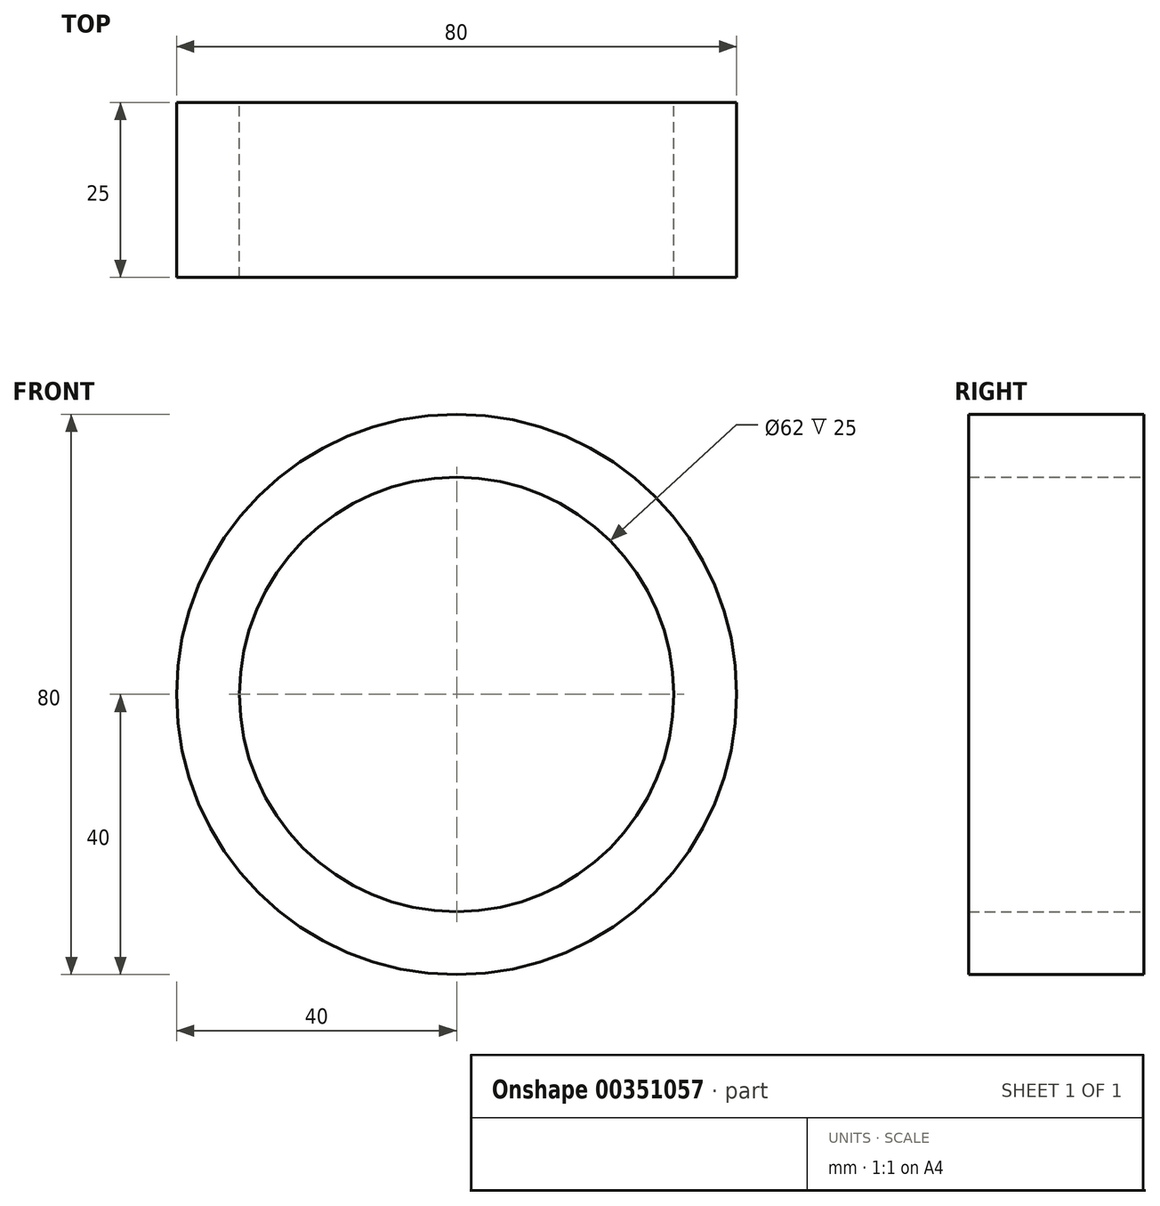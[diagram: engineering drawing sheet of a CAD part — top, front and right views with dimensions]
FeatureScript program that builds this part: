
annotation { "Feature Type Name" : "Feature", "Feature Type Description" : "" }
export const myFeature = defineFeature(function(context is Context, id is Id, definition is map)
    precondition{}
    {
        {
            var Q0;
            Q0=qCreatedBy(makeId("Front.planeOp"),FACE);
            var sketch = newSketch(context, id + "F0", { "sketchPlane" : qUnion([Q0])});
            skCircle(sketch, "E0", {"center": v(0, 0) * mm, "radius": 40 * mm});
            skCircle(sketch, "E1", {"center": v(0, 0) * mm, "radius": 31 * mm});
            skCircle(sketch, "E2", {"center": v(0, 0) * mm, "radius": 7.5 * mm});
            skCircle(sketch, "E3", {"center": v(0, 0) * mm, "radius": 2.5 * mm});
            skLineSegment(sketch, "E4", {"start": v(0, 0) * mm, "end": v(0, 40) * mm});
            skLineSegment(sketch, "E5", {"start": v(0, 0) * mm, "end": v(40, 0) * mm});
            skLineSegment(sketch, "E6", {"start": v(0, 0) * mm, "end": v(0, -40) * mm});
            skLineSegment(sketch, "E7", {"start": v(0, 0) * mm, "end": v(-40, 0) * mm});
            skLineSegment(sketch, "E8.0", {"start": v(5, 0) * mm, "end": v(5, 40) * mm});
            skLineSegment(sketch, "E9.0", {"start": v(-5, 0) * mm, "end": v(-5, 40) * mm});
            skLineSegment(sketch, "E10.0", {"start": v(0, 5) * mm, "end": v(-40, 5) * mm});
            skLineSegment(sketch, "E11.0", {"start": v(0, -5) * mm, "end": v(-40, -5) * mm});
            skLineSegment(sketch, "E12.0", {"start": v(-5, 0) * mm, "end": v(-5, -40) * mm});
            skLineSegment(sketch, "E13.0", {"start": v(5, 0) * mm, "end": v(5, -40) * mm});
            skLineSegment(sketch, "E14.0", {"start": v(0, -5) * mm, "end": v(40, -5) * mm});
            skLineSegment(sketch, "E15.0", {"start": v(0, 5) * mm, "end": v(40, 5) * mm});
            skSolve(sketch);
        }
        {
            var Q0;
            {var subQ0=sQuery(id+"F0.wireOp",EDGE,"E4");var subQ1=sQuery(id+"F0.wireOp",EDGE,"E0");var subQ2=makeQuery(id+"F0.imprint","INTERSECT",VERTEX,{"derivedFrom":[subQ1,subQ0]});Q0=makeQuery(id+"F0.imprint","IMPRINT",FACE,{"disambiguationData":[TD([[makeQuery(id+"F0.imprint","IMPRINT",EDGE,{"disambiguationData":[TD([[subQ2,1.0]])],"derivedFrom":subQ1}),1.0]])]});}
            var Q1;
            {var subQ0=sQuery(id+"F0.wireOp",EDGE,"E4");var subQ1=sQuery(id+"F0.wireOp",EDGE,"E0");var subQ2=makeQuery(id+"F0.imprint","INTERSECT",VERTEX,{"derivedFrom":[subQ1,subQ0]});Q1=makeQuery(id+"F0.imprint","IMPRINT",FACE,{"disambiguationData":[TD([[makeQuery(id+"F0.imprint","IMPRINT",EDGE,{"disambiguationData":[TD([[subQ2,-1.0]])],"derivedFrom":subQ1}),1.0]])]});}
            var Q2;
            {var subQ0=sQuery(id+"F0.wireOp",EDGE,"E9.0");var subQ1=sQuery(id+"F0.wireOp",EDGE,"E0");var subQ2=makeQuery(id+"F0.imprint","INTERSECT",VERTEX,{"derivedFrom":[subQ1,subQ0]});Q2=makeQuery(id+"F0.imprint","IMPRINT",FACE,{"disambiguationData":[TD([[makeQuery(id+"F0.imprint","IMPRINT",EDGE,{"disambiguationData":[TD([[subQ2,-1.0]])],"derivedFrom":subQ1}),1.0]])]});}
            var Q3;
            {var subQ0=sQuery(id+"F0.wireOp",EDGE,"E7");var subQ1=sQuery(id+"F0.wireOp",EDGE,"E0");var subQ2=makeQuery(id+"F0.imprint","INTERSECT",VERTEX,{"derivedFrom":[subQ1,subQ0]});Q3=makeQuery(id+"F0.imprint","IMPRINT",FACE,{"disambiguationData":[TD([[makeQuery(id+"F0.imprint","IMPRINT",EDGE,{"disambiguationData":[TD([[subQ2,1.0]])],"derivedFrom":subQ1}),1.0]])]});}
            var Q4;
            {var subQ0=sQuery(id+"F0.wireOp",EDGE,"E7");var subQ1=sQuery(id+"F0.wireOp",EDGE,"E0");var subQ2=makeQuery(id+"F0.imprint","INTERSECT",VERTEX,{"derivedFrom":[subQ1,subQ0]});Q4=makeQuery(id+"F0.imprint","IMPRINT",FACE,{"disambiguationData":[TD([[makeQuery(id+"F0.imprint","IMPRINT",EDGE,{"disambiguationData":[TD([[subQ2,-1.0]])],"derivedFrom":subQ1}),1.0]])]});}
            var Q5;
            {var subQ0=sQuery(id+"F0.wireOp",EDGE,"E11.0");var subQ1=sQuery(id+"F0.wireOp",EDGE,"E0");var subQ2=makeQuery(id+"F0.imprint","INTERSECT",VERTEX,{"derivedFrom":[subQ1,subQ0]});Q5=makeQuery(id+"F0.imprint","IMPRINT",FACE,{"disambiguationData":[TD([[makeQuery(id+"F0.imprint","IMPRINT",EDGE,{"disambiguationData":[TD([[subQ2,-1.0]])],"derivedFrom":subQ1}),1.0]])]});}
            var Q6;
            {var subQ0=sQuery(id+"F0.wireOp",EDGE,"E6");var subQ1=sQuery(id+"F0.wireOp",EDGE,"E0");var subQ2=makeQuery(id+"F0.imprint","INTERSECT",VERTEX,{"derivedFrom":[subQ1,subQ0]});Q6=makeQuery(id+"F0.imprint","IMPRINT",FACE,{"disambiguationData":[TD([[makeQuery(id+"F0.imprint","IMPRINT",EDGE,{"disambiguationData":[TD([[subQ2,1.0]])],"derivedFrom":subQ1}),1.0]])]});}
            var Q7;
            {var subQ0=sQuery(id+"F0.wireOp",EDGE,"E6");var subQ1=sQuery(id+"F0.wireOp",EDGE,"E0");var subQ2=makeQuery(id+"F0.imprint","INTERSECT",VERTEX,{"derivedFrom":[subQ1,subQ0]});Q7=makeQuery(id+"F0.imprint","IMPRINT",FACE,{"disambiguationData":[TD([[makeQuery(id+"F0.imprint","IMPRINT",EDGE,{"disambiguationData":[TD([[subQ2,-1.0]])],"derivedFrom":subQ1}),1.0]])]});}
            var Q8;
            {var subQ0=sQuery(id+"F0.wireOp",EDGE,"E13.0");var subQ1=sQuery(id+"F0.wireOp",EDGE,"E0");var subQ2=makeQuery(id+"F0.imprint","INTERSECT",VERTEX,{"derivedFrom":[subQ1,subQ0]});Q8=makeQuery(id+"F0.imprint","IMPRINT",FACE,{"disambiguationData":[TD([[makeQuery(id+"F0.imprint","IMPRINT",EDGE,{"disambiguationData":[TD([[subQ2,-1.0]])],"derivedFrom":subQ1}),1.0]])]});}
            var Q9;
            {var subQ0=sQuery(id+"F0.wireOp",EDGE,"E5");var subQ1=sQuery(id+"F0.wireOp",EDGE,"E0");var subQ2=makeQuery(id+"F0.imprint","INTERSECT",VERTEX,{"derivedFrom":[subQ1,subQ0]});Q9=makeQuery(id+"F0.imprint","IMPRINT",FACE,{"disambiguationData":[TD([[makeQuery(id+"F0.imprint","IMPRINT",EDGE,{"disambiguationData":[TD([[subQ2,1.0]])],"derivedFrom":subQ1}),1.0]])]});}
            var Q10;
            {var subQ0=sQuery(id+"F0.wireOp",EDGE,"E5");var subQ1=sQuery(id+"F0.wireOp",EDGE,"E0");var subQ2=makeQuery(id+"F0.imprint","INTERSECT",VERTEX,{"derivedFrom":[subQ1,subQ0]});Q10=makeQuery(id+"F0.imprint","IMPRINT",FACE,{"disambiguationData":[TD([[makeQuery(id+"F0.imprint","IMPRINT",EDGE,{"disambiguationData":[TD([[subQ2,-1.0]])],"derivedFrom":subQ1}),1.0]])]});}
            var Q11;
            {var subQ0=sQuery(id+"F0.wireOp",EDGE,"E15.0");var subQ1=sQuery(id+"F0.wireOp",EDGE,"E0");var subQ2=makeQuery(id+"F0.imprint","INTERSECT",VERTEX,{"derivedFrom":[subQ1,subQ0]});Q11=makeQuery(id+"F0.imprint","IMPRINT",FACE,{"disambiguationData":[TD([[makeQuery(id+"F0.imprint","IMPRINT",EDGE,{"disambiguationData":[TD([[subQ2,-1.0]])],"derivedFrom":subQ1}),1.0]])]});}
            extrude(context, id + "F1", {"entities" : qUnion([Q0, Q1, Q2, Q3, Q4, Q5, Q6, Q7, Q8, Q9, Q10, Q11]), "depth" : 25 * mm});
        }
    });
